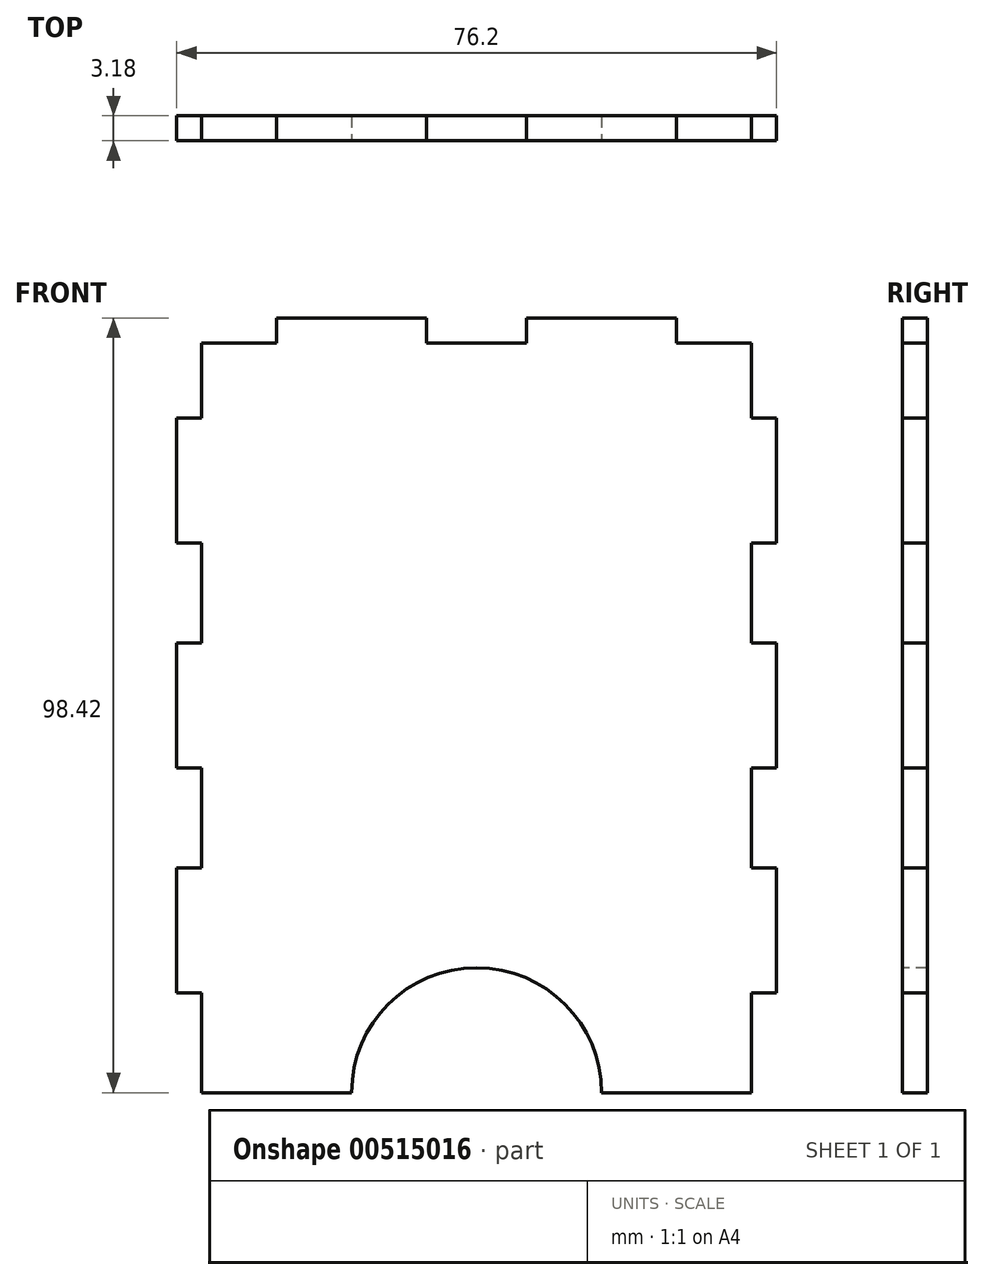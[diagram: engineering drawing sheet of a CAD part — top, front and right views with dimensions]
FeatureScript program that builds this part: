
annotation { "Feature Type Name" : "Feature", "Feature Type Description" : "" }
export const myFeature = defineFeature(function(context is Context, id is Id, definition is map)
    precondition{}
    {
        {
            var Q0;
            Q0=qCreatedBy(makeId("Front.planeOp"),FACE);
            var sketch = newSketch(context, id + "F0", { "sketchPlane" : qUnion([Q0])});
            skLineSegment(sketch, "E0.bottom", {"start": v(-38.1, 49.21) * mm, "end": v(38.1, 49.21) * mm});
            skLineSegment(sketch, "E0.top", {"start": v(-38.1, -49.21) * mm, "end": v(38.1, -49.21) * mm});
            skLineSegment(sketch, "E0.left", {"start": v(-38.1, 49.21) * mm, "end": v(-38.1, -49.21) * mm});
            skLineSegment(sketch, "E0.right", {"start": v(38.1, 49.21) * mm, "end": v(38.1, -49.21) * mm});
            skSolve(sketch);
        }
        {
            var Q0;
            Q0=makeQuery(id+"F0.imprint","IMPRINT",FACE,{"disambiguationData":[TD([[makeQuery(id+"F0.imprint","IMPRINT",EDGE,{"derivedFrom":sQuery(id+"F0.wireOp",EDGE,"E0.bottom")}),-1.0]])]});
            extrude(context, id + "F1", {"entities" : qUnion([Q0]), "depth" : 3.17 * mm, "offsetDistance" : 25.4 * mm});
        }
        {
            var Q0;
            Q0=makeQuery(id+"F1.opExtrude","CAP_FACE",FACE,{"disambiguationData":[OSD([sQuery(id+"F0.wireOp",EDGE,"E0.bottom"),sQuery(id+"F0.wireOp",EDGE,"E0.top"),sQuery(id+"F0.wireOp",EDGE,"E0.left"),sQuery(id+"F0.wireOp",EDGE,"E0.right")])],"isStart":false});
            var sketch = newSketch(context, id + "F2", { "sketchPlane" : qUnion([Q0])});
            skLineSegment(sketch, "E1.bottom", {"start": v(-38.1, 49.21) * mm, "end": v(-25.4, 49.21) * mm});
            skLineSegment(sketch, "E1.top", {"start": v(-38.1, 46.04) * mm, "end": v(-25.4, 46.04) * mm});
            skLineSegment(sketch, "E1.left", {"start": v(-38.1, 49.21) * mm, "end": v(-38.1, 46.04) * mm});
            skLineSegment(sketch, "E1.right", {"start": v(-25.4, 49.21) * mm, "end": v(-25.4, 46.04) * mm});
            skLineSegment(sketch, "E2.1.0.0", {"start": v(6.35, 49.21) * mm, "end": v(6.35, 46.04) * mm});
            skLineSegment(sketch, "E2.1.0.1", {"start": v(-6.35, 49.21) * mm, "end": v(-6.35, 46.04) * mm});
            skLineSegment(sketch, "E2.1.0.2", {"start": v(-6.35, 46.04) * mm, "end": v(6.35, 46.04) * mm});
            skLineSegment(sketch, "E2.1.0.3", {"start": v(-6.35, 49.21) * mm, "end": v(6.35, 49.21) * mm});
            skLineSegment(sketch, "E2.direction1", {"start": v(-38.1, 46.04) * mm, "end": v(-6.35, 46.04) * mm, "construction": true});
            skLineSegment(sketch, "E3.0.2.0", {"start": v(38.1, 49.21) * mm, "end": v(38.1, 46.04) * mm});
            skLineSegment(sketch, "E3.3.2.0", {"start": v(25.4, 49.21) * mm, "end": v(25.4, 46.04) * mm});
            skLineSegment(sketch, "E3.6.2.0", {"start": v(25.4, 46.04) * mm, "end": v(38.1, 46.04) * mm});
            skLineSegment(sketch, "E3.9.2.0", {"start": v(25.4, 49.21) * mm, "end": v(38.1, 49.21) * mm});
            skSolve(sketch);
        }
        {
            var Q0;
            Q0 = qSketchRegion(id + "F2", true);
            extrude(context, id + "F3", {"entities" : qUnion([Q0]), "operationType" : NewBodyOperationType.REMOVE, "endBound" : BoundingType.THROUGH_ALL, "oppositeDirection" : true, "depth" : 25.4 * mm, "offsetDistance" : 25.4 * mm});
        }
        {
            var Q0;
            Q0=makeQuery(id+"F1.opExtrude","CAP_FACE",FACE,{"disambiguationData":[OSD([sQuery(id+"F0.wireOp",EDGE,"E0.bottom"),sQuery(id+"F0.wireOp",EDGE,"E0.top"),sQuery(id+"F0.wireOp",EDGE,"E0.left"),sQuery(id+"F0.wireOp",EDGE,"E0.right")])],"isStart":false});
            var sketch = newSketch(context, id + "F4", { "sketchPlane" : qUnion([Q0])});
            skLineSegment(sketch, "E4.bottom", {"start": v(-38.1, 49.21) * mm, "end": v(-34.93, 49.21) * mm});
            skLineSegment(sketch, "E4.top", {"start": v(-38.1, 36.51) * mm, "end": v(-34.93, 36.51) * mm});
            skLineSegment(sketch, "E4.left", {"start": v(-38.1, 49.21) * mm, "end": v(-38.1, 36.51) * mm});
            skLineSegment(sketch, "E4.right", {"start": v(-34.93, 49.21) * mm, "end": v(-34.93, 36.51) * mm});
            skLineSegment(sketch, "E5.0.1.0", {"start": v(-38.1, 20.64) * mm, "end": v(-34.93, 20.64) * mm});
            skLineSegment(sketch, "E5.0.1.1", {"start": v(-38.1, 7.94) * mm, "end": v(-34.93, 7.94) * mm});
            skLineSegment(sketch, "E5.0.1.2", {"start": v(-38.1, 20.64) * mm, "end": v(-38.1, 7.94) * mm});
            skLineSegment(sketch, "E5.0.1.3", {"start": v(-34.93, 20.64) * mm, "end": v(-34.93, 7.94) * mm});
            skLineSegment(sketch, "E5.0.2.0", {"start": v(-38.1, -7.94) * mm, "end": v(-34.93, -7.94) * mm});
            skLineSegment(sketch, "E5.0.2.1", {"start": v(-38.1, -20.64) * mm, "end": v(-34.93, -20.64) * mm});
            skLineSegment(sketch, "E5.0.2.2", {"start": v(-38.1, -7.94) * mm, "end": v(-38.1, -20.64) * mm});
            skLineSegment(sketch, "E5.0.2.3", {"start": v(-34.93, -7.94) * mm, "end": v(-34.93, -20.64) * mm});
            skLineSegment(sketch, "E5.0.3.0", {"start": v(-38.1, -36.51) * mm, "end": v(-34.93, -36.51) * mm});
            skLineSegment(sketch, "E5.0.3.1", {"start": v(-38.1, -49.21) * mm, "end": v(-34.93, -49.21) * mm});
            skLineSegment(sketch, "E5.0.3.2", {"start": v(-38.1, -36.51) * mm, "end": v(-38.1, -49.21) * mm});
            skLineSegment(sketch, "E5.0.3.3", {"start": v(-34.93, -36.51) * mm, "end": v(-34.93, -49.21) * mm});
            skLineSegment(sketch, "E5.direction1", {"start": v(-38.1, 36.51) * mm, "end": v(-2.13, 36.51) * mm, "construction": true});
            skLineSegment(sketch, "E5.direction2", {"start": v(-38.1, 36.51) * mm, "end": v(-38.1, 7.94) * mm, "construction": true});
            skLineSegment(sketch, "E6", {"start": v(0, 46.04) * mm, "end": v(0, -49.21) * mm, "construction": true});
            skLineSegment(sketch, "E7.MirrorCS", {"start": v(38.1, -36.51) * mm, "end": v(34.92, -36.51) * mm});
            skLineSegment(sketch, "E8.MirrorCS", {"start": v(38.1, 20.64) * mm, "end": v(34.92, 20.64) * mm});
            skLineSegment(sketch, "E9.MirrorCS", {"start": v(38.1, -20.64) * mm, "end": v(34.92, -20.64) * mm});
            skLineSegment(sketch, "E10.MirrorCS", {"start": v(38.1, 49.21) * mm, "end": v(34.92, 49.21) * mm});
            skLineSegment(sketch, "E11.MirrorCS", {"start": v(38.1, 36.51) * mm, "end": v(34.92, 36.51) * mm});
            skLineSegment(sketch, "E12.MirrorCS", {"start": v(38.1, -49.21) * mm, "end": v(34.92, -49.21) * mm});
            skLineSegment(sketch, "E13.MirrorCS", {"start": v(38.1, -7.94) * mm, "end": v(34.92, -7.94) * mm});
            skLineSegment(sketch, "E14.MirrorCS", {"start": v(38.1, 7.94) * mm, "end": v(34.92, 7.94) * mm});
            skLineSegment(sketch, "E15.MirrorCS", {"start": v(38.1, 20.64) * mm, "end": v(38.1, 7.94) * mm});
            skLineSegment(sketch, "E16.MirrorCS", {"start": v(38.1, -36.51) * mm, "end": v(38.1, -49.21) * mm});
            skLineSegment(sketch, "E17.MirrorCS", {"start": v(38.1, 49.21) * mm, "end": v(38.1, 36.51) * mm});
            skLineSegment(sketch, "E18.MirrorCS", {"start": v(38.1, 36.51) * mm, "end": v(38.1, 7.94) * mm, "construction": true});
            skLineSegment(sketch, "E19.MirrorCS", {"start": v(38.1, 36.51) * mm, "end": v(2.13, 36.51) * mm, "construction": true});
            skLineSegment(sketch, "E20.MirrorCS", {"start": v(34.92, -7.94) * mm, "end": v(34.92, -20.64) * mm});
            skLineSegment(sketch, "E21.MirrorCS", {"start": v(34.92, 49.21) * mm, "end": v(34.92, 36.51) * mm});
            skLineSegment(sketch, "E22.MirrorCS", {"start": v(38.1, -7.94) * mm, "end": v(38.1, -20.64) * mm});
            skLineSegment(sketch, "E23.MirrorCS", {"start": v(34.92, 20.64) * mm, "end": v(34.92, 7.94) * mm});
            skLineSegment(sketch, "E24.MirrorCS", {"start": v(34.92, -36.51) * mm, "end": v(34.92, -49.21) * mm});
            skSolve(sketch);
        }
        {
            var Q0;
            Q0 = qSketchRegion(id + "F4", true);
            extrude(context, id + "F5", {"entities" : qUnion([Q0]), "operationType" : NewBodyOperationType.REMOVE, "endBound" : BoundingType.THROUGH_ALL, "oppositeDirection" : true, "depth" : 25.4 * mm, "offsetDistance" : 25.4 * mm});
        }
        {
            var Q0;
            Q0=makeQuery(id+"F1.opExtrude","CAP_FACE",FACE,{"disambiguationData":[OSD([sQuery(id+"F0.wireOp",EDGE,"E0.bottom"),sQuery(id+"F0.wireOp",EDGE,"E0.top"),sQuery(id+"F0.wireOp",EDGE,"E0.left"),sQuery(id+"F0.wireOp",EDGE,"E0.right")])],"isStart":false});
            var sketch = newSketch(context, id + "F6", { "sketchPlane" : qUnion([Q0])});
            skEllipse(sketch, "E25", {"center": v(0, -49.21) * mm, "majorRadius": 15.88 * mm, "minorRadius": 15.88 * mm, "majorAxis": v(1, 0)});
            skSolve(sketch);
        }
        {
            var Q0;
            Q0 = qSketchRegion(id + "F6", true);
            extrude(context, id + "F7", {"entities" : qUnion([Q0]), "operationType" : NewBodyOperationType.REMOVE, "endBound" : BoundingType.THROUGH_ALL, "oppositeDirection" : true, "depth" : 25.4 * mm, "offsetDistance" : 25.4 * mm});
        }
    });
